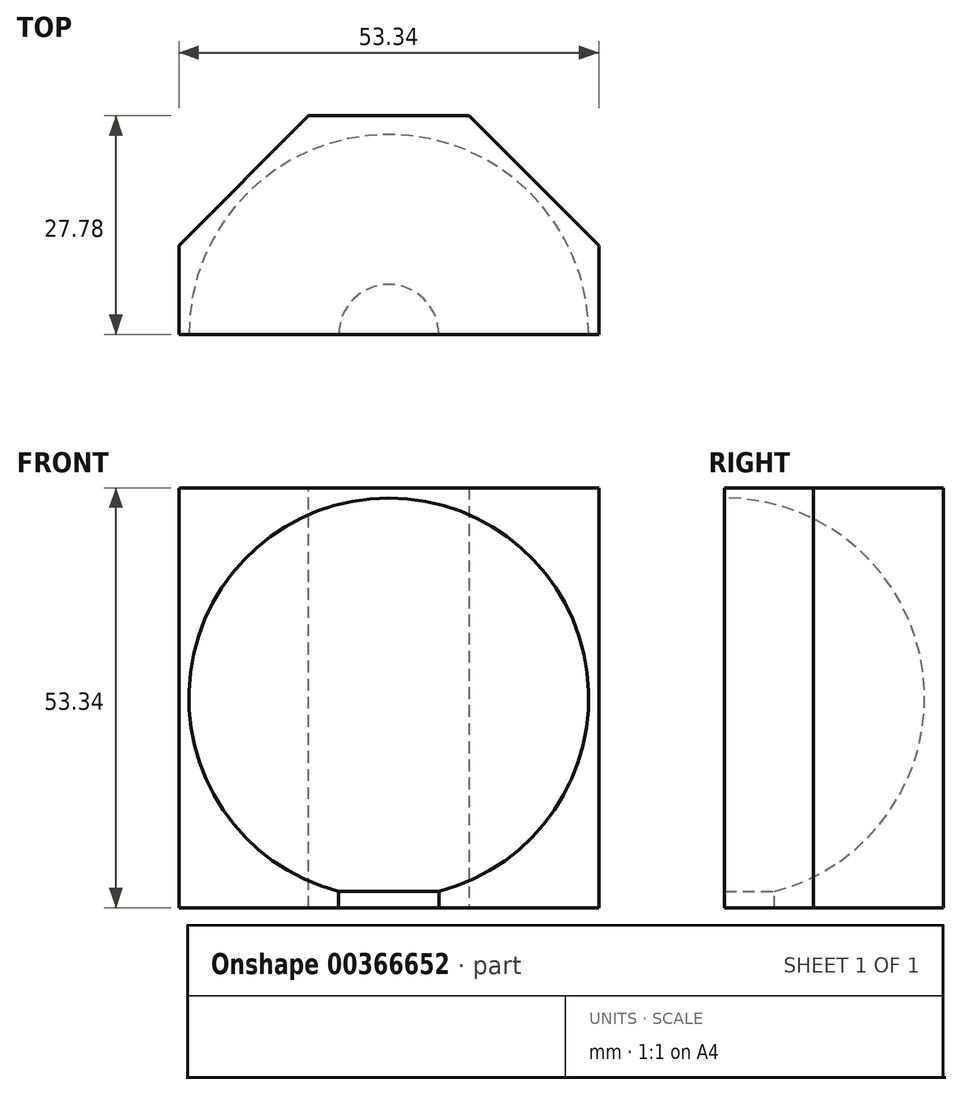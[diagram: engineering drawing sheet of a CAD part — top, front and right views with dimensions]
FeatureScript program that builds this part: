
annotation { "Feature Type Name" : "Feature", "Feature Type Description" : "" }
export const myFeature = defineFeature(function(context is Context, id is Id, definition is map)
    precondition{}
    {
        {
            var Q0;
            Q0=qCreatedBy(makeId("Front.planeOp"),FACE);
            var sketch = newSketch(context, id + "F0", { "sketchPlane" : qUnion([Q0])});
            skLineSegment(sketch, "E0.bottom", {"start": v(26.67, 26.67) * mm, "end": v(-26.67, 26.67) * mm});
            skLineSegment(sketch, "E0.top", {"start": v(26.67, -26.67) * mm, "end": v(-26.67, -26.67) * mm});
            skLineSegment(sketch, "E0.left", {"start": v(26.67, 26.67) * mm, "end": v(26.67, -26.67) * mm});
            skLineSegment(sketch, "E0.right", {"start": v(-26.67, 26.67) * mm, "end": v(-26.67, -26.67) * mm});
            skPoint(sketch, "E0.middle", {"position": v(0, 0) * mm});
            skCircle(sketch, "E1", {"center": v(0, 0) * mm, "radius": 25.4 * mm});
            skLineSegment(sketch, "E2", {"start": v(0, -25.4) * mm, "end": v(0, 25.4) * mm});
            skPoint(sketch, "E2.startSnap0", {"position": v(0, -26.67) * mm});
            skSolve(sketch);
        }
        {
            var Q0;
            {var subQ0=sQuery(id+"F0.wireOp",EDGE,"E2");Q0=makeQuery(id+"F0.imprint","IMPRINT",FACE,{"disambiguationData":[TD([[makeQuery(id+"F0.imprint","IMPRINT",EDGE,{"derivedFrom":subQ0}),1.0]])]});}
            var Q1;
            {var subQ0=sQuery(id+"F0.wireOp",EDGE,"E2");Q1=makeQuery(id+"F0.imprint","IMPRINT",FACE,{"disambiguationData":[TD([[makeQuery(id+"F0.imprint","IMPRINT",EDGE,{"derivedFrom":subQ0}),-1.0]])]});}
            var Q2;
            Q2=makeQuery(id+"F0.imprint","IMPRINT",FACE,{"disambiguationData":[TD([[makeQuery(id+"F0.imprint","IMPRINT",EDGE,{"derivedFrom":sQuery(id+"F0.wireOp",EDGE,"E0.bottom")}),1.0]])]});
            extrude(context, id + "F1", {"entities" : qUnion([Q0, Q1, Q2]), "oppositeDirection" : true, "depth" : 27.78 * mm});
        }
        {
            var Q0;
            {var subQ0=sQuery(id+"F0.wireOp",EDGE,"E2");Q0=makeQuery(id+"F0.imprint","IMPRINT",FACE,{"disambiguationData":[TD([[makeQuery(id+"F0.imprint","IMPRINT",EDGE,{"derivedFrom":subQ0}),-1.0]])]});}
            var Q1;
            Q1=sQuery(id+"F0.wireOp",EDGE,"E2");
            revolve(context, id + "F2", {"operationType" : NewBodyOperationType.REMOVE, "entities" : qUnion([Q0]), "axis" : qUnion([Q1]), "revolveType" : RevolveType.FULL});
        }
        {
            var Q0;
            Q0=qCreatedBy(makeId("Top.planeOp"),FACE);
            var sketch = newSketch(context, id + "F3", { "sketchPlane" : qUnion([Q0])});
            skCircle(sketch, "E3", {"center": v(0, 0) * mm, "radius": 6.35 * mm});
            skSolve(sketch);
        }
        {
            var Q0;
            Q0 = qSketchRegion(id + "F3", true);
            extrude(context, id + "F4", {"entities" : qUnion([Q0]), "operationType" : NewBodyOperationType.REMOVE, "oppositeDirection" : true, "depth" : 38.1 * mm});
        }
        {
            var Q0;
            Q0=makeQuery(id+"F1.opExtrude","CAP_EDGE",EDGE,{"disambiguationData":[OSD([sQuery(id+"F0.wireOp",EDGE,"E0.left")])],"isStart":false});
            chamfer(context, id + "F5", {"entities" : qUnion([Q0]), "width" : 16.5 * mm, "tangentPropagation" : true});
        }
        {
            var Q0;
            Q0=makeQuery(id+"F1.opExtrude","CAP_EDGE",EDGE,{"disambiguationData":[OSD([sQuery(id+"F0.wireOp",EDGE,"E0.right")])],"isStart":false});
            chamfer(context, id + "F6", {"entities" : qUnion([Q0]), "width" : 16.5 * mm, "tangentPropagation" : true});
        }
    });
